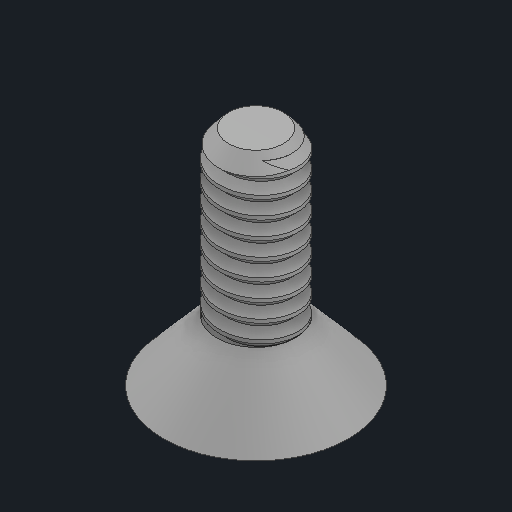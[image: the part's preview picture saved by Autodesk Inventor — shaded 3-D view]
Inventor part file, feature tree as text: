
AUTODESK INVENTOR PART (.ipt)
format: ipt  version: 2025 (Build 290162000, 162)  size: 343,040 bytes
history: native  units: in
note: dims shown in document units (in); Inventor stores cm internally (conversion verified against a paired STEP export)
features: extrude x1
ambient origin geometry x8: Origin, YZ Plane, XZ Plane, XY Plane, X Axis, Y Axis, Z Axis, Center Point
bodies: Solid1 (feature_tree)
feature tree (1):
  extrude  "Extrude4"  [1 undecoded]
note: 1 required parameter value undecoded (feature->parameter linkage not recoverable at this tier; creation-order binding heuristic only, values carry confidence <= 0.55)
